# Revit family: LCAT-CM
name_source: partatom
category: Lighting Fixtures
revit_build: Autodesk Revit MEP 2012 (Build: 20110916_2132(x64)
units: mm (PartAtom-declared; Revit-internal decimal feet)

## types (3) — shared parameters
Apparent Load = 0 VA
Backbox = Hubbell - White
Default Elevation = 4.000'
Description = LCAT provides both design and value with an architectural appearance, LED technology to reduce maintenance and a wide range of options for classrooms, offices, retail and health care applications
Lamp = LED Lamp
Light Bulb = Hubbell - White Glass
Manufacturer = Columbia Lighting
Manufacturer Fax = (866)-898-1065
Product Documentation Link = http://cdn.columbialighting.com
Product Page URL = http://www.columbialighting.com
Suspension Height = 2.000'
URL = http://www.columbialighting.com
Voltage = 120 V
Warranty = Five year warranty
Wattage Comments = 40-80 W

## per-type parameters (varying)
| type | Load Classification | Photometric Web | Row Length | Width | zz Length |
| LCAT-CM-14 | Lighting | Web LCAT : LCAT14-30HLG-EDU | 4.000' | 1.000' | 3.917' |
| LCAT-CM-22 | Other | Web LCAT : LCAT22-50HLG-EDU | 2.000' | 1.979' | 1.917' |
| LCAT-CM-24 | Lighting | Web LCAT : LCAT24-35LWG-EDU | 4.000' | 2.083' | 3.917' |

note: column(s) folded — value = type name in every type: Model

## geometry (parser evidence)
native form markers: Sweep x8
no freeform markers — native parametric forms only
